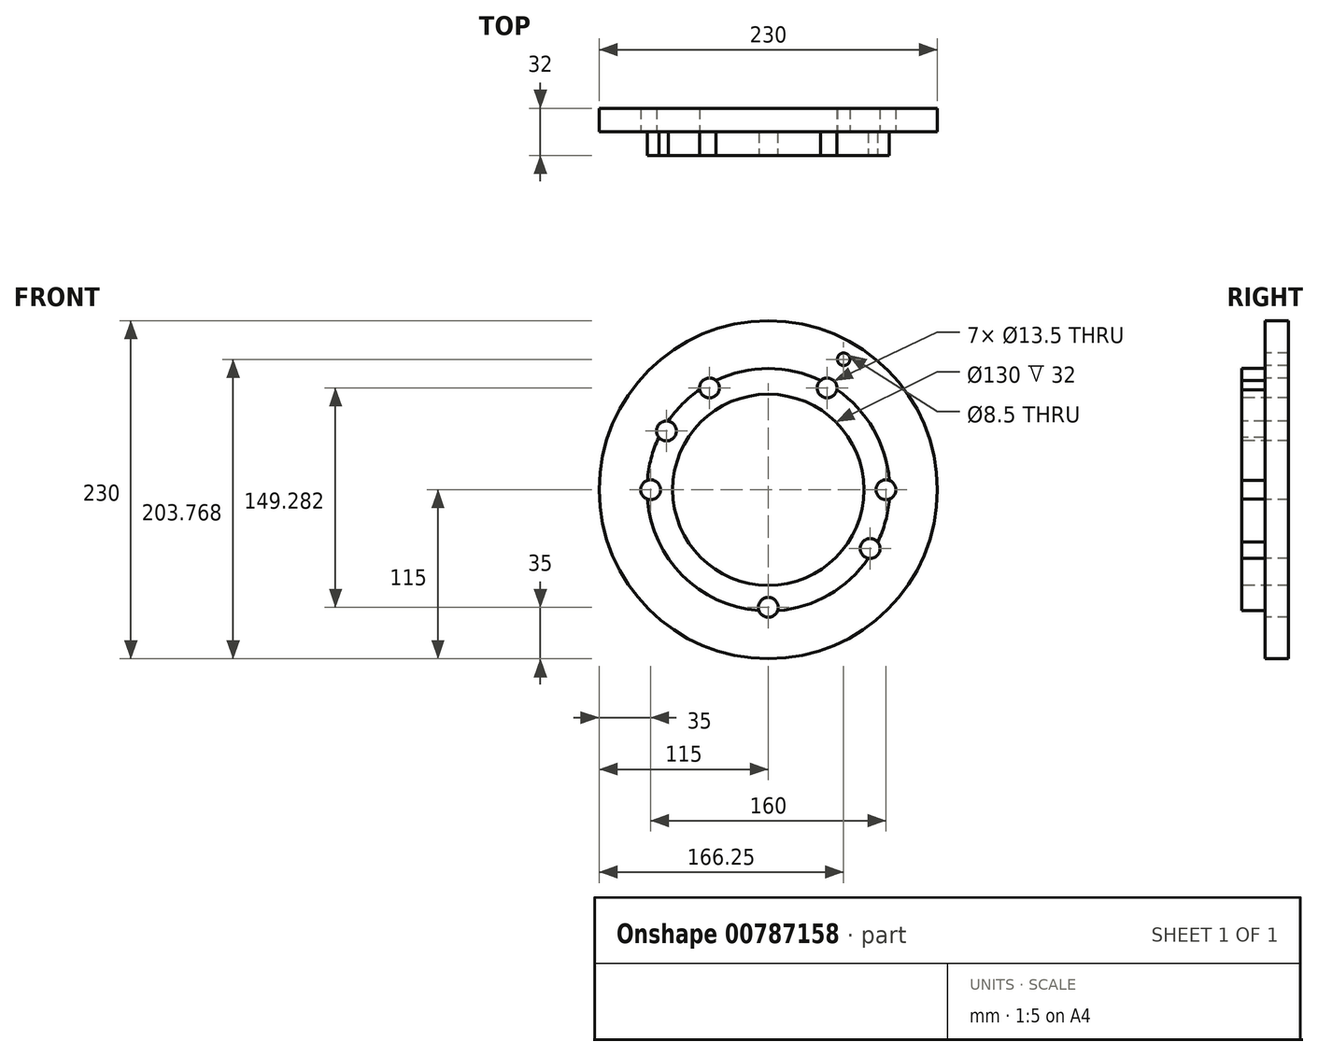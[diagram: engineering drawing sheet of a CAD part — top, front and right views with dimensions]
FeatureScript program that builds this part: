
annotation { "Feature Type Name" : "Feature", "Feature Type Description" : "" }
export const myFeature = defineFeature(function(context is Context, id is Id, definition is map)
    precondition{}
    {
        {
            var Q0;
            Q0=qCreatedBy(makeId("Front.planeOp"),FACE);
            var sketch = newSketch(context, id + "F0", { "sketchPlane" : qUnion([Q0])});
            skCircle(sketch, "E0", {"center": v(0, 0) * mm, "radius": 115 * mm});
            skSolve(sketch);
        }
        {
            var Q0;
            Q0=makeQuery(id+"F0.imprint","IMPRINT",FACE,{"disambiguationData":[TD([[makeQuery(id+"F0.imprint","IMPRINT",EDGE,{"derivedFrom":sQuery(id+"F0.wireOp",EDGE,"E0")}),1.0]])]});
            extrude(context, id + "F1", {"entities" : qUnion([Q0]), "depth" : 16 * mm, "offsetDistance" : 25 * mm});
        }
        {
            var Q0;
            Q0=makeQuery(id+"F1.opExtrude","CAP_FACE",FACE,{"disambiguationData":[OSD([sQuery(id+"F0.wireOp",EDGE,"E0")])],"isStart":false});
            var sketch = newSketch(context, id + "F2", { "sketchPlane" : qUnion([Q0])});
            skCircle(sketch, "E1", {"center": v(0, 0) * mm, "radius": 82.5 * mm});
            skSolve(sketch);
        }
        {
            var Q0;
            Q0=makeQuery(id+"F2.imprint","IMPRINT",FACE,{"disambiguationData":[TD([[makeQuery(id+"F2.imprint","IMPRINT",EDGE,{"derivedFrom":sQuery(id+"F2.wireOp",EDGE,"E1")}),1.0]])]});
            extrude(context, id + "F3", {"entities" : qUnion([Q0]), "operationType" : NewBodyOperationType.ADD, "depth" : 16 * mm, "offsetDistance" : 25 * mm});
        }
        {
            var Q0;
            Q0=makeQuery(id+"F3.opExtrude","CAP_FACE",FACE,{"disambiguationData":[OSD([sQuery(id+"F2.wireOp",EDGE,"E1")])],"isStart":false});
            var sketch = newSketch(context, id + "F4", { "sketchPlane" : qUnion([Q0])});
            skCircle(sketch, "E2", {"center": v(0, 0) * mm, "radius": 65 * mm});
            skSolve(sketch);
        }
        {
            var Q0;
            Q0=makeQuery(id+"F4.imprint","IMPRINT",FACE,{"disambiguationData":[TD([[makeQuery(id+"F4.imprint","IMPRINT",EDGE,{"derivedFrom":sQuery(id+"F4.wireOp",EDGE,"E2")}),1.0]])]});
            extrude(context, id + "F5", {"entities" : qUnion([Q0]), "operationType" : NewBodyOperationType.REMOVE, "endBound" : BoundingType.THROUGH_ALL, "oppositeDirection" : true, "depth" : 25 * mm, "offsetDistance" : 25 * mm});
        }
        {
            var Q0;
            Q0=makeQuery(id+"F3.opExtrude","CAP_FACE",FACE,{"disambiguationData":[OSD([sQuery(id+"F2.wireOp",EDGE,"E1")])],"isStart":false});
            var sketch = newSketch(context, id + "F6", { "sketchPlane" : qUnion([Q0])});
            skCircle(sketch, "E3", {"center": v(0, 0) * mm, "radius": 80 * mm, "construction": true});
            skLineSegment(sketch, "E4", {"start": v(0, 0) * mm, "end": v(0, 80) * mm, "construction": true});
            skLineSegment(sketch, "E5", {"start": v(0, 0) * mm, "end": v(40, 69.28) * mm, "construction": true});
            skLineSegment(sketch, "E6", {"start": v(0, 0) * mm, "end": v(80, 0) * mm, "construction": true});
            skLineSegment(sketch, "E7", {"start": v(0, 0) * mm, "end": v(69.28, -40) * mm, "construction": true});
            skLineSegment(sketch, "E8", {"start": v(0, 0) * mm, "end": v(0, -80) * mm, "construction": true});
            skLineSegment(sketch, "E9", {"start": v(0, 0) * mm, "end": v(-80, 0) * mm, "construction": true});
            skLineSegment(sketch, "E10", {"start": v(0, 0) * mm, "end": v(-69.28, 40) * mm, "construction": true});
            skLineSegment(sketch, "E11", {"start": v(0, 0) * mm, "end": v(-40, 69.28) * mm, "construction": true});
            skSolve(sketch);
        }
        {
            var Q0;
            Q0=sQuery(id+"F6.wireOp",VERTEX,"E5.end");
            var Q1;
            Q1=sQuery(id+"F6.wireOp",VERTEX,"E6.end");
            var Q2;
            Q2=sQuery(id+"F6.wireOp",VERTEX,"E7.end");
            var Q3;
            Q3=sQuery(id+"F6.wireOp",VERTEX,"E8.end");
            var Q4;
            Q4=sQuery(id+"F6.wireOp",VERTEX,"E9.end");
            var Q5;
            Q5=sQuery(id+"F6.wireOp",VERTEX,"E10.end");
            var Q6;
            Q6=sQuery(id+"F6.wireOp",VERTEX,"E11.end");
            var Q7;
            Q7=makeQuery(id+"F1.opExtrude","SWEPT_BODY",BODY,{"disambiguationData":[OSD([sQuery(id+"F0.wireOp",EDGE,"E0")])]});
            hole(context, id + "F7", {"style" : HoleStyle.SIMPLE, "endStyle" : HoleEndStyle.THROUGH, "holeDiameter" : 13.5 * mm, "majorDiameter" : 10 * mm, "isTappedThrough" : true, "tappedDepth" : 12 * mm, "tapClearance" : 3, "locations" : qUnion([Q0, Q1, Q2, Q3, Q4, Q5, Q6]), "scope" : qUnion([Q7])});
        }
        {
            var Q0;
            Q0=makeQuery(id+"F1.opExtrude","CAP_FACE",FACE,{"disambiguationData":[OSD([sQuery(id+"F0.wireOp",EDGE,"E0")])],"isStart":false});
            var sketch = newSketch(context, id + "F8", { "sketchPlane" : qUnion([Q0])});
            skCircle(sketch, "E12", {"center": v(0, 0) * mm, "radius": 102.5 * mm, "construction": true});
            skLineSegment(sketch, "E13", {"start": v(0, 0) * mm, "end": v(0, 102.5) * mm, "construction": true});
            skLineSegment(sketch, "E14", {"start": v(0, 0) * mm, "end": v(51.25, 88.77) * mm, "construction": true});
            skSolve(sketch);
        }
        {
            var Q0;
            Q0=sQuery(id+"F8.wireOp",VERTEX,"E14.end");
            var Q1;
            Q1=makeQuery(id+"F1.opExtrude","SWEPT_BODY",BODY,{"disambiguationData":[OSD([sQuery(id+"F0.wireOp",EDGE,"E0")])]});
            hole(context, id + "F9", {"style" : HoleStyle.SIMPLE, "endStyle" : HoleEndStyle.THROUGH, "standardTappedOrClearance" : lookupTablePath({ "standard" : "ISO", "engagement" : "75%", "pitch" : "1.5 mm", "size" : "M10", "type" : "Tapped" }), "standardBlindInLast" : lookupTablePath({ "standard" : "ISO", "engagement" : "75%", "pitch" : "1.5 mm", "size" : "M10", "type" : "Tapped" }), "holeDiameter" : 8.5 * mm, "majorDiameter" : 10 * mm, "showTappedDepth" : true, "isTappedThrough" : true, "tappedDepth" : 12 * mm, "tapClearance" : 3, "locations" : qUnion([Q0]), "scope" : qUnion([Q1])});
        }
    });
